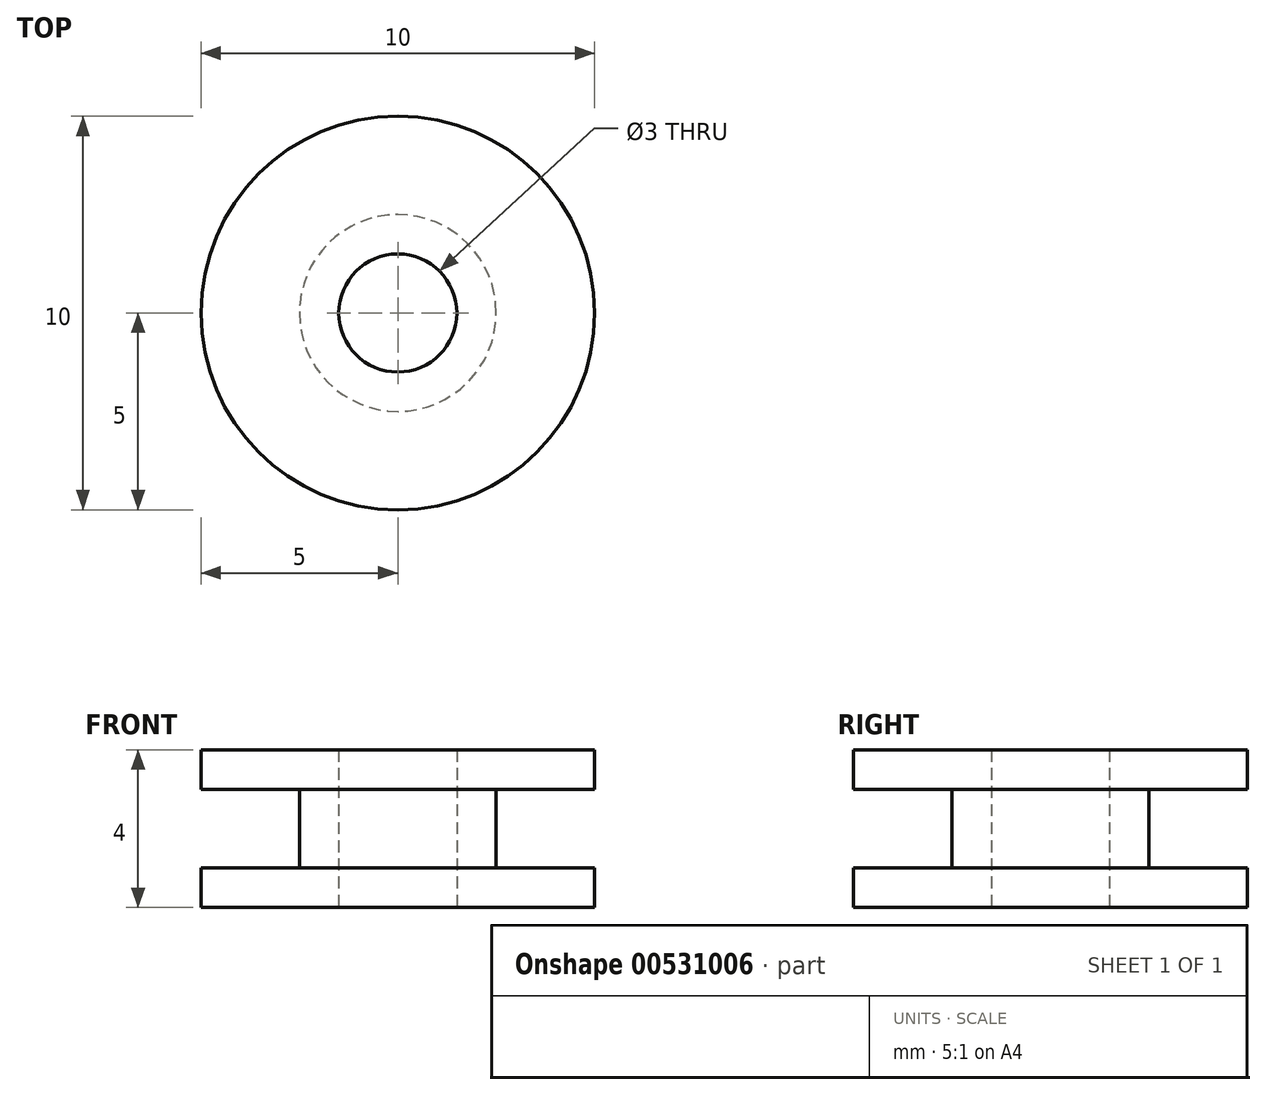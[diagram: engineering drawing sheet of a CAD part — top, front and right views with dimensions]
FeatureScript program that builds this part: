
annotation { "Feature Type Name" : "Feature", "Feature Type Description" : "" }
export const myFeature = defineFeature(function(context is Context, id is Id, definition is map)
    precondition{}
    {
        {
            var Q0;
            Q0=qCreatedBy(makeId("Top.planeOp"),FACE);
            var sketch = newSketch(context, id + "F0", { "sketchPlane" : qUnion([Q0])});
            skCircle(sketch, "E0", {"center": v(0, 0) * mm, "radius": 1.5 * mm});
            skCircle(sketch, "E1", {"center": v(0, 0) * mm, "radius": 2.5 * mm});
            skCircle(sketch, "E2", {"center": v(0, 0) * mm, "radius": 5 * mm});
            skSolve(sketch);
        }
        {
            var Q0;
            Q0=makeQuery(id+"F0.imprint","IMPRINT",FACE,{"disambiguationData":[TD([[makeQuery(id+"F0.imprint","IMPRINT",EDGE,{"derivedFrom":sQuery(id+"F0.wireOp",EDGE,"E0")}),-1.0]])]});
            extrude(context, id + "F1", {"entities" : qUnion([Q0]), "depth" : 4 * mm, "offsetDistance" : 25 * mm});
        }
        {
            var Q0;
            Q0=makeQuery(id+"F0.imprint","IMPRINT",FACE,{"disambiguationData":[TD([[makeQuery(id+"F0.imprint","IMPRINT",EDGE,{"derivedFrom":sQuery(id+"F0.wireOp",EDGE,"E1")}),-1.0]])]});
            extrude(context, id + "F2", {"entities" : qUnion([Q0]), "operationType" : NewBodyOperationType.ADD, "depth" : 1 * mm, "offsetDistance" : 25 * mm});
        }
        {
            var Q0;
            Q0=makeQuery(id+"F1.opExtrude","CAP_FACE",FACE,{"disambiguationData":[OSD([sQuery(id+"F0.wireOp",EDGE,"E0"),sQuery(id+"F0.wireOp",EDGE,"E1")])],"isStart":false});
            var sketch = newSketch(context, id + "F3", { "sketchPlane" : qUnion([Q0])});
            skCircle(sketch, "E3", {"center": v(0, 0) * mm, "radius": 5 * mm});
            skSolve(sketch);
        }
        {
            var Q0;
            Q0=makeQuery(id+"F3.imprint","IMPRINT",FACE,{"disambiguationData":[TD([[makeQuery(id+"F3.imprint","IMPRINT",EDGE,{"derivedFrom":sQuery(id+"F3.wireOp",EDGE,"E3")}),1.0]])]});
            var Q1;
            Q1=makeQuery(id+"F3.imprint","IMPRINT",FACE,{"disambiguationData":[TD([[makeQuery(id+"F3.imprint","IMPRINT",EDGE,{"derivedFrom":makeQuery(id+"F1.opExtrude","CAP_EDGE",EDGE,{"disambiguationData":[OSD([sQuery(id+"F0.wireOp",EDGE,"E0")])],"isStart":false})}),-1.0]])]});
            extrude(context, id + "F4", {"entities" : qUnion([Q0, Q1]), "operationType" : NewBodyOperationType.ADD, "oppositeDirection" : true, "depth" : 1 * mm, "offsetDistance" : 25 * mm});
        }
    });
